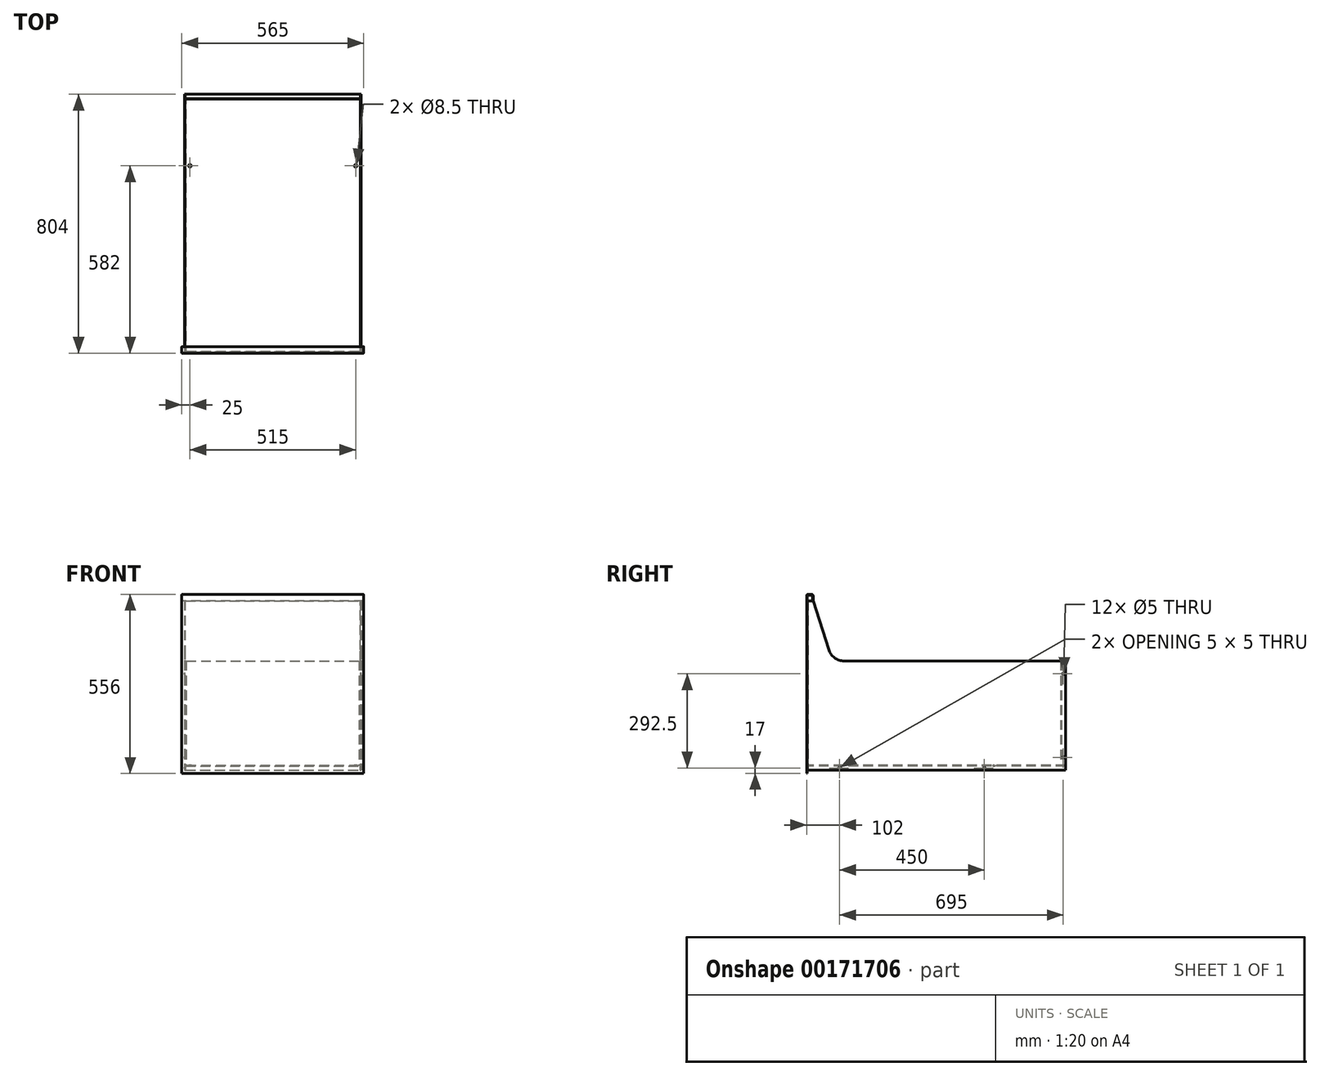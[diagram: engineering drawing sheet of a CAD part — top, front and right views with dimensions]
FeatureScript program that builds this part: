
annotation { "Feature Type Name" : "Feature", "Feature Type Description" : "" }
export const myFeature = defineFeature(function(context is Context, id is Id, definition is map)
    precondition{}
    {
        {
            var Q0;
            Q0=qCreatedBy(makeId("Top.planeOp"),FACE);
            var sketch = newSketch(context, id + "F0", { "sketchPlane" : qUnion([Q0])});
            skLineSegment(sketch, "E0.top", {"start": v(-270.5, -401) * mm, "end": v(270.5, -401) * mm});
            skLineSegment(sketch, "E0.left", {"start": v(-274.5, 401) * mm, "end": v(-274.5, -397) * mm});
            skLineSegment(sketch, "E0.right", {"start": v(274.5, 401) * mm, "end": v(274.5, -397) * mm});
            skPoint(sketch, "E0.middle", {"position": v(0, 0) * mm});
            skLineSegment(sketch, "E1", {"start": v(-274.5, 401) * mm, "end": v(274.5, 401) * mm, "construction": true});
            skLineSegment(sketch, "E2", {"start": v(-274.5, 401) * mm, "end": v(-272.5, 401) * mm});
            skLineSegment(sketch, "E3", {"start": v(-272.5, 401) * mm, "end": v(-272.5, -399) * mm});
            skLineSegment(sketch, "E4", {"start": v(-272.5, -399) * mm, "end": v(272.5, -399) * mm});
            skLineSegment(sketch, "E5", {"start": v(272.5, -399) * mm, "end": v(272.5, 401) * mm});
            skPoint(sketch, "E6.visualSharp", {"position": v(-274.5, -401) * mm});
            skArc(sketch, "E6.filletArc", {"start": v(-274.5, -397) * mm, "mid": v(-273.33, -399.83) * mm, "end": v(-270.5, -401) * mm});
            skPoint(sketch, "E7.visualSharp", {"position": v(274.5, -401) * mm});
            skArc(sketch, "E7.filletArc", {"start": v(270.5, -401) * mm, "mid": v(273.33, -399.83) * mm, "end": v(274.5, -397) * mm});
            skLineSegment(sketch, "E8", {"start": v(272.5, 401) * mm, "end": v(274.5, 401) * mm});
            skSolve(sketch);
        }
        {
            var Q0;
            Q0=makeQuery(id+"F0.imprint","IMPRINT",FACE,{"disambiguationData":[TD([[makeQuery(id+"F0.imprint","IMPRINT",EDGE,{"derivedFrom":sQuery(id+"F0.wireOp",EDGE,"E0.top")}),1.0]])]});
            extrude(context, id + "F1", {"entities" : qUnion([Q0]), "depth" : 526 * mm});
        }
        {
            var Q0;
            Q0=makeQuery(id+"F1.opExtrude","SWEPT_FACE",FACE,{"disambiguationData":[OSD([sQuery(id+"F0.wireOp",EDGE,"E4")])]});
            var sketch = newSketch(context, id + "F2", { "sketchPlane" : qUnion([Q0])});
            skLineSegment(sketch, "E9", {"start": v(-272.5, 0) * mm, "end": v(-272.5, 11) * mm});
            skLineSegment(sketch, "E10", {"start": v(-268.5, 15) * mm, "end": v(268.5, 15) * mm});
            skLineSegment(sketch, "E11", {"start": v(272.5, 11) * mm, "end": v(272.5, 0) * mm});
            skLineSegment(sketch, "E12", {"start": v(272.5, 0) * mm, "end": v(270.5, 0) * mm});
            skLineSegment(sketch, "E13", {"start": v(270.5, 0) * mm, "end": v(270.5, 13) * mm});
            skLineSegment(sketch, "E14", {"start": v(270.5, 13) * mm, "end": v(-270.5, 13) * mm});
            skLineSegment(sketch, "E15", {"start": v(-270.5, 13) * mm, "end": v(-270.5, 0) * mm});
            skLineSegment(sketch, "E16", {"start": v(-270.5, 0) * mm, "end": v(-272.5, 0) * mm});
            skPoint(sketch, "E17.visualSharp", {"position": v(272.5, 15) * mm});
            skArc(sketch, "E17.filletArc", {"start": v(272.5, 11) * mm, "mid": v(271.33, 13.83) * mm, "end": v(268.5, 15) * mm});
            skPoint(sketch, "E18.visualSharp", {"position": v(-272.5, 15) * mm});
            skArc(sketch, "E18.filletArc", {"start": v(-268.5, 15) * mm, "mid": v(-271.33, 13.83) * mm, "end": v(-272.5, 11) * mm});
            skSolve(sketch);
        }
        {
            var Q0;
            Q0=makeQuery(id+"F2.imprint","IMPRINT",FACE,{"disambiguationData":[TD([[makeQuery(id+"F2.imprint","IMPRINT",EDGE,{"derivedFrom":sQuery(id+"F2.wireOp",EDGE,"E9")}),1.0]])]});
            var Q1;
            Q1=makeQuery(id+"F1.opExtrude","SWEPT_FACE",FACE,{"disambiguationData":[OSD([sQuery(id+"F0.wireOp",EDGE,"E2")])]});
            extrude(context, id + "F3", {"entities" : qUnion([Q0]), "endBound" : BoundingType.UP_TO_SURFACE, "endBoundEntityFace" : qUnion([Q1]), "depth" : 25 * mm});
        }
        {
            var Q0;
            Q0=makeQuery(id+"F3.opExtrude","SWEPT_FACE",FACE,{"disambiguationData":[OSD([sQuery(id+"F2.wireOp",EDGE,"E10")])]});
            var sketch = newSketch(context, id + "F4", { "sketchPlane" : qUnion([Q0])});
            skLineSegment(sketch, "E19.0", {"start": v(272.5, -399) * mm, "end": v(272.5, 401) * mm});
            skLineSegment(sketch, "E20.0", {"start": v(-272.5, 401) * mm, "end": v(-272.5, -399) * mm});
            skLineSegment(sketch, "E21", {"start": v(-272.5, 401) * mm, "end": v(-272.5, 390) * mm});
            skLineSegment(sketch, "E22", {"start": v(-268.5, 386) * mm, "end": v(268.5, 386) * mm});
            skLineSegment(sketch, "E23", {"start": v(272.5, 390) * mm, "end": v(272.5, 401) * mm});
            skLineSegment(sketch, "E24", {"start": v(272.5, 401) * mm, "end": v(270.5, 401) * mm});
            skLineSegment(sketch, "E25", {"start": v(270.5, 401) * mm, "end": v(270.5, 388) * mm});
            skLineSegment(sketch, "E26", {"start": v(270.5, 388) * mm, "end": v(-270.5, 388) * mm});
            skLineSegment(sketch, "E27", {"start": v(-270.5, 388) * mm, "end": v(-270.5, 401) * mm});
            skLineSegment(sketch, "E28", {"start": v(-270.5, 401) * mm, "end": v(-272.5, 401) * mm});
            skPoint(sketch, "E29.visualSharp", {"position": v(272.5, 386) * mm});
            skArc(sketch, "E29.filletArc", {"start": v(268.5, 386) * mm, "mid": v(271.33, 387.17) * mm, "end": v(272.5, 390) * mm});
            skPoint(sketch, "E30.visualSharp", {"position": v(-272.5, 386) * mm});
            skArc(sketch, "E30.filletArc", {"start": v(-272.5, 390) * mm, "mid": v(-271.33, 387.17) * mm, "end": v(-268.5, 386) * mm});
            skSolve(sketch);
        }
        {
            var Q0;
            {var subQ0=sQuery(id+"F4.wireOp",EDGE,"E22");Q0=makeQuery(id+"F4.imprint","IMPRINT",FACE,{"disambiguationData":[TD([[makeQuery(id+"F4.imprint","IMPRINT",EDGE,{"derivedFrom":subQ0}),1.0]])]});}
            var Q1;
            Q1=makeQuery(id+"F4.imprint","IMPRINT",FACE,{"disambiguationData":[TD([[makeQuery(id+"F4.imprint","IMPRINT",EDGE,{"derivedFrom":sQuery(id+"F4.wireOp",EDGE,"E21")}),1.0]])]});
            var Q2;
            Q2=makeQuery(id+"F4.imprint","IMPRINT",FACE,{"disambiguationData":[TD([[makeQuery(id+"F4.imprint","IMPRINT",EDGE,{"derivedFrom":sQuery(id+"F4.wireOp",EDGE,"E23")}),1.0]])]});
            extrude(context, id + "F5", {"entities" : qUnion([Q0, Q1, Q2]), "depth" : 324.5 * mm});
        }
        {
            var Q0;
            Q0=makeQuery(id+"F1.opExtrude","SWEPT_FACE",FACE,{"disambiguationData":[OSD([sQuery(id+"F0.wireOp",EDGE,"E0.right")])]});
            var sketch = newSketch(context, id + "F6", { "sketchPlane" : qUnion([Q0])});
            skLineSegment(sketch, "E31.0", {"start": v(-401, 526) * mm, "end": v(-401, 0) * mm});
            skLineSegment(sketch, "E32", {"start": v(-374.1, 7) * mm, "end": v(407.57, 7) * mm, "construction": true});
            skLineSegment(sketch, "E33", {"start": v(394, -59.87) * mm, "end": v(394, 378.9) * mm, "construction": true});
            skPoint(sketch, "E34", {"position": v(-301, 7) * mm});
            skPoint(sketch, "E35", {"position": v(149, 7) * mm});
            skPoint(sketch, "E36", {"position": v(394, 299.5) * mm});
            skPoint(sketch, "E37", {"position": v(394, 40) * mm});
            skLineSegment(sketch, "E38.0", {"start": v(390, 339.5) * mm, "end": v(401, 339.5) * mm});
            skLineSegment(sketch, "E39", {"start": v(-401, 526) * mm, "end": v(-383, 526) * mm});
            skLineSegment(sketch, "E40", {"start": v(-383, 526) * mm, "end": v(-334.64, 374.31) * mm});
            skLineSegment(sketch, "E41", {"start": v(-287, 339.5) * mm, "end": v(390, 339.5) * mm});
            skPoint(sketch, "E42.visualSharp", {"position": v(-323.54, 339.5) * mm});
            skArc(sketch, "E42.filletArc", {"start": v(-334.64, 374.31) * mm, "mid": v(-316.5, 349.13) * mm, "end": v(-287, 339.5) * mm});
            skSolve(sketch);
        }
        {
            var Q0;
            Q0=sQuery(id+"F6.wireOp",VERTEX,"E37");
            var Q1;
            Q1=sQuery(id+"F6.wireOp",VERTEX,"E35");
            var Q2;
            Q2=sQuery(id+"F6.wireOp",VERTEX,"E36");
            var Q3;
            Q3=sQuery(id+"F6.wireOp",VERTEX,"E34");
            var Q4;
            Q4=makeQuery(id+"F1.opExtrude","SWEPT_BODY",BODY,{"disambiguationData":[OSD([sQuery(id+"F0.wireOp",EDGE,"E0.top"),sQuery(id+"F0.wireOp",EDGE,"E0.left"),sQuery(id+"F0.wireOp",EDGE,"E0.right"),sQuery(id+"F0.wireOp",EDGE,"E2"),sQuery(id+"F0.wireOp",EDGE,"E3"),sQuery(id+"F0.wireOp",EDGE,"E4"),sQuery(id+"F0.wireOp",EDGE,"E5"),sQuery(id+"F0.wireOp",EDGE,"E6.filletArc"),sQuery(id+"F0.wireOp",EDGE,"E7.filletArc"),sQuery(id+"F0.wireOp",EDGE,"E8")])]});
            var Q5;
            Q5=makeQuery(id+"F3.opExtrude","SWEPT_BODY",BODY,{"disambiguationData":[OSD([sQuery(id+"F2.wireOp",EDGE,"E9"),sQuery(id+"F2.wireOp",EDGE,"E10"),sQuery(id+"F2.wireOp",EDGE,"E11"),sQuery(id+"F2.wireOp",EDGE,"E12"),sQuery(id+"F2.wireOp",EDGE,"E13"),sQuery(id+"F2.wireOp",EDGE,"E14"),sQuery(id+"F2.wireOp",EDGE,"E15"),sQuery(id+"F2.wireOp",EDGE,"E16"),sQuery(id+"F2.wireOp",EDGE,"E17.filletArc"),sQuery(id+"F2.wireOp",EDGE,"E18.filletArc")])]});
            var Q6;
            Q6=makeQuery(id+"F5.opExtrude","SWEPT_BODY",BODY,{"disambiguationData":[OSD([sQuery(id+"F4.wireOp",EDGE,"E21"),sQuery(id+"F4.wireOp",EDGE,"E22"),sQuery(id+"F4.wireOp",EDGE,"E23"),sQuery(id+"F4.wireOp",EDGE,"E24"),sQuery(id+"F4.wireOp",EDGE,"E25"),sQuery(id+"F4.wireOp",EDGE,"E26"),sQuery(id+"F4.wireOp",EDGE,"E27"),sQuery(id+"F4.wireOp",EDGE,"E28"),sQuery(id+"F4.wireOp",EDGE,"E29.filletArc"),sQuery(id+"F4.wireOp",EDGE,"E30.filletArc")])]});
            hole(context, id + "F7", {"style" : HoleStyle.C_SINK, "endStyle" : HoleEndStyle.BLIND, "holeDiameter" : 5 * mm, "cSinkDiameter" : 5 * mm, "cSinkAngle" : 90 * degree, "holeDepth" : 2000 * mm, "startFromSketch" : true, "locations" : qUnion([Q0, Q1, Q2, Q3]), "scope" : qUnion([Q4, Q5, Q6])});
        }
        {
            var Q0;
            Q0=qCreatedBy(makeId("Right.planeOp"),FACE);
            var sketch = newSketch(context, id + "F8", { "sketchPlane" : qUnion([Q0])});
            skPoint(sketch, "E43.0", {"position": v(-401, 526) * mm});
            skPoint(sketch, "E44.0", {"position": v(-401, 0) * mm});
            skLineSegment(sketch, "E45.0", {"start": v(401, 526) * mm, "end": v(-397, 526) * mm});
            skLineSegment(sketch, "E46", {"start": v(-401, 526) * mm, "end": v(-401, 544) * mm});
            skLineSegment(sketch, "E47", {"start": v(-401, 544) * mm, "end": v(-385, 544) * mm});
            skLineSegment(sketch, "E48", {"start": v(-385, 544) * mm, "end": v(-385, 526) * mm});
            skLineSegment(sketch, "E49", {"start": v(-385, 526) * mm, "end": v(-383, 526) * mm});
            skLineSegment(sketch, "E50", {"start": v(-383, 526) * mm, "end": v(-383, 542) * mm});
            skLineSegment(sketch, "E51", {"start": v(-387, 546) * mm, "end": v(-399, 546) * mm});
            skLineSegment(sketch, "E52", {"start": v(-403, 542) * mm, "end": v(-403, 526) * mm});
            skLineSegment(sketch, "E53", {"start": v(-403, 526) * mm, "end": v(-401, 526) * mm});
            skPoint(sketch, "E54.visualSharp", {"position": v(-403, 546) * mm});
            skArc(sketch, "E54.filletArc", {"start": v(-399, 546) * mm, "mid": v(-401.83, 544.83) * mm, "end": v(-403, 542) * mm});
            skPoint(sketch, "E55.visualSharp", {"position": v(-383, 546) * mm});
            skArc(sketch, "E55.filletArc", {"start": v(-383, 542) * mm, "mid": v(-384.17, 544.83) * mm, "end": v(-387, 546) * mm});
            skLineSegment(sketch, "E56", {"start": v(-401, 0) * mm, "end": v(-401, -10) * mm});
            skLineSegment(sketch, "E57", {"start": v(-401, -10) * mm, "end": v(-403, -10) * mm});
            skLineSegment(sketch, "E58", {"start": v(-403, -10) * mm, "end": v(-403, 0) * mm});
            skLineSegment(sketch, "E59", {"start": v(-403, 0) * mm, "end": v(-401, 0) * mm});
            skLineSegment(sketch, "E60", {"start": v(-401, 0) * mm, "end": v(-401, 526) * mm});
            skLineSegment(sketch, "E61", {"start": v(-403, 526) * mm, "end": v(-403, 0) * mm});
            skSolve(sketch);
        }
        {
            var Q0;
            Q0=makeQuery(id+"F8.imprint","IMPRINT",FACE,{"disambiguationData":[TD([[makeQuery(id+"F8.imprint","IMPRINT",EDGE,{"derivedFrom":sQuery(id+"F8.wireOp",EDGE,"E56")}),-1.0]])]});
            var Q1;
            Q1=makeQuery(id+"F8.imprint","IMPRINT",FACE,{"disambiguationData":[TD([[makeQuery(id+"F8.imprint","IMPRINT",EDGE,{"derivedFrom":sQuery(id+"F8.wireOp",EDGE,"E53")}),-1.0]])]});
            var Q2;
            Q2=makeQuery(id+"F8.imprint","IMPRINT",FACE,{"disambiguationData":[TD([[makeQuery(id+"F8.imprint","IMPRINT",EDGE,{"derivedFrom":sQuery(id+"F8.wireOp",EDGE,"E46")}),1.0]])]});
            extrude(context, id + "F9", {"entities" : qUnion([Q0, Q1, Q2]), "endBound" : BoundingType.SYMMETRIC, "depth" : 565 * mm});
        }
        {
            var Q0;
            {var subQ5=sQuery(id+"F6.wireOp",EDGE,"E38.0");Q0=makeQuery(id+"F6.imprint","IMPRINT",FACE,{"disambiguationData":[TD([[makeQuery(id+"F6.imprint","IMPRINT",EDGE,{"derivedFrom":subQ5}),1.0]])]});}
            extrude(context, id + "F10", {"entities" : qUnion([Q0]), "operationType" : NewBodyOperationType.REMOVE, "oppositeDirection" : true, "depth" : 1000 * mm});
        }
        {
            var Q0;
            Q0=makeQuery(id+"F3.opExtrude","SWEPT_FACE",FACE,{"disambiguationData":[OSD([sQuery(id+"F2.wireOp",EDGE,"E14")])]});
            var sketch = newSketch(context, id + "F11", { "sketchPlane" : qUnion([Q0])});
            skLineSegment(sketch, "E62", {"start": v(424.17, -179) * mm, "end": v(-480.87, -179) * mm, "construction": true});
            skPoint(sketch, "E63", {"position": v(257.5, -179) * mm});
            skLineSegment(sketch, "E64.0", {"start": v(272.5, 399) * mm, "end": v(272.5, -401) * mm});
            skLineSegment(sketch, "E65.0", {"start": v(-272.5, -401) * mm, "end": v(-272.5, 399) * mm});
            skPoint(sketch, "E66", {"position": v(-257.5, -179) * mm});
            skSolve(sketch);
        }
        {
            var Q0;
            Q0=sQuery(id+"F11.wireOp",VERTEX,"E63");
            var Q1;
            Q1=sQuery(id+"F11.wireOp",VERTEX,"E66");
            var Q2;
            Q2=makeQuery(id+"F3.opExtrude","SWEPT_BODY",BODY,{"disambiguationData":[OSD([sQuery(id+"F2.wireOp",EDGE,"E9"),sQuery(id+"F2.wireOp",EDGE,"E10"),sQuery(id+"F2.wireOp",EDGE,"E11"),sQuery(id+"F2.wireOp",EDGE,"E12"),sQuery(id+"F2.wireOp",EDGE,"E13"),sQuery(id+"F2.wireOp",EDGE,"E14"),sQuery(id+"F2.wireOp",EDGE,"E15"),sQuery(id+"F2.wireOp",EDGE,"E16"),sQuery(id+"F2.wireOp",EDGE,"E17.filletArc"),sQuery(id+"F2.wireOp",EDGE,"E18.filletArc")])]});
            hole(context, id + "F12", {"style" : HoleStyle.C_SINK, "endStyle" : HoleEndStyle.BLIND, "holeDiameter" : 8.5 * mm, "cSinkDiameter" : 8.5 * mm, "cSinkAngle" : 90 * degree, "holeDepth" : 20 * mm, "startFromSketch" : true, "locations" : qUnion([Q0, Q1]), "scope" : qUnion([Q2])});
        }
    });
